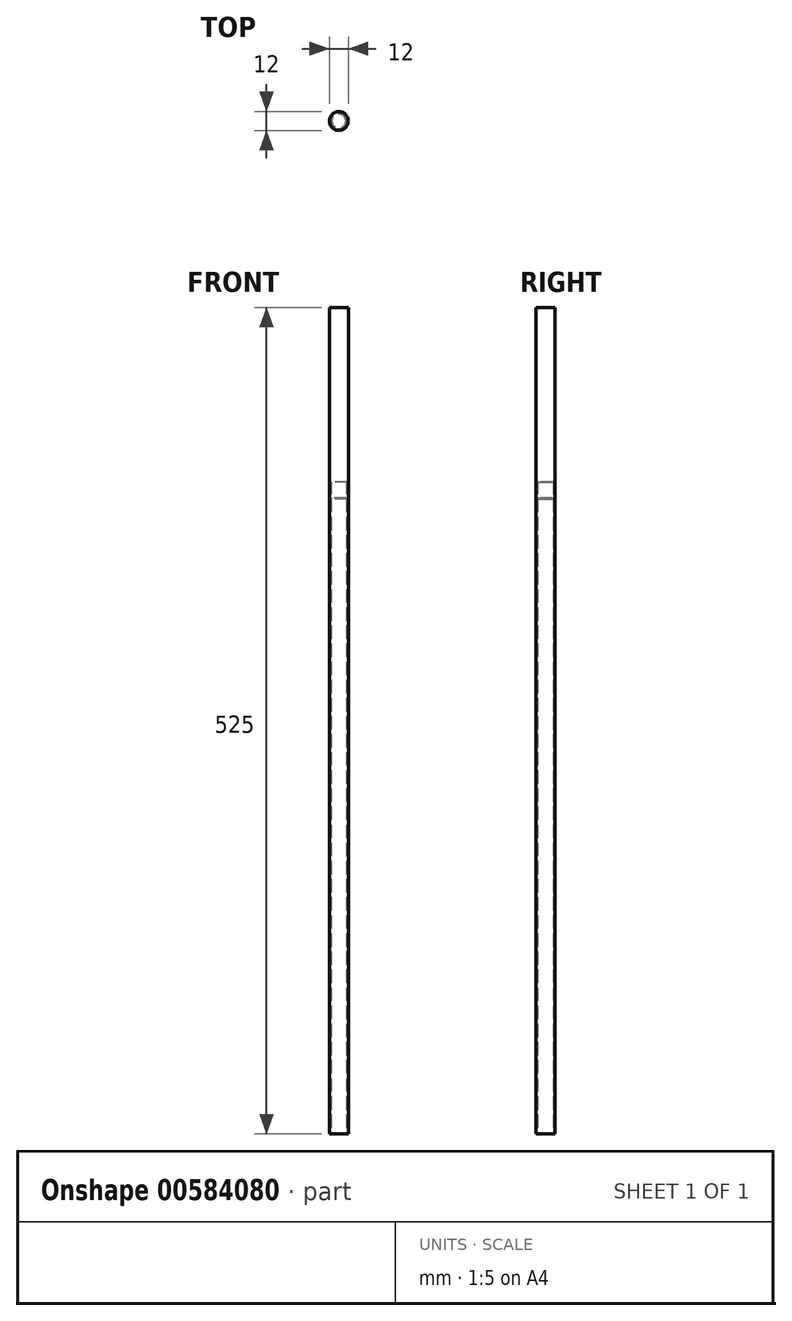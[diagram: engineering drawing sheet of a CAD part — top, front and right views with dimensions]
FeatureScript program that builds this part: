
annotation { "Feature Type Name" : "Feature", "Feature Type Description" : "" }
export const myFeature = defineFeature(function(context is Context, id is Id, definition is map)
    precondition{}
    {
        {
            var Q0;
            Q0=qCreatedBy(makeId("Top.planeOp"),FACE);
            var sketch = newSketch(context, id + "F0", { "sketchPlane" : qUnion([Q0])});
            skCircle(sketch, "E0", {"center": v(0, 0) * mm, "radius": 5 * mm});
            skCircle(sketch, "E1", {"center": v(0, 0) * mm, "radius": 6 * mm});
            skSolve(sketch);
        }
        {
            var Q0;
            Q0=makeQuery(id+"F0.imprint","IMPRINT",FACE,{"disambiguationData":[TD([[makeQuery(id+"F0.imprint","IMPRINT",EDGE,{"derivedFrom":sQuery(id+"F0.wireOp",EDGE,"E0")}),1.0]])]});
            var Q1;
            Q1=makeQuery(id+"F0.imprint","IMPRINT",FACE,{"disambiguationData":[TD([[makeQuery(id+"F0.imprint","IMPRINT",EDGE,{"derivedFrom":sQuery(id+"F0.wireOp",EDGE,"E0")}),-1.0]])]});
            extrude(context, id + "F1", {"entities" : qUnion([Q0, Q1]), "depth" : 525 * mm, "offsetDistance" : 25 * mm});
        }
        {
            var Q0;
            Q0=makeQuery(id+"F0.imprint","IMPRINT",FACE,{"disambiguationData":[TD([[makeQuery(id+"F0.imprint","IMPRINT",EDGE,{"derivedFrom":sQuery(id+"F0.wireOp",EDGE,"E0")}),1.0]])]});
            extrude(context, id + "F2", {"entities" : qUnion([Q0]), "depth" : 404 * mm, "offsetDistance" : 25 * mm});
        }
        {
            var Q0;
            Q0=makeQuery(id+"F1.opExtrude","CAP_EDGE",EDGE,{"disambiguationData":[OSD([sQuery(id+"F0.wireOp",EDGE,"E0")])],"isStart":false});
            var Q1;
            Q1=makeQuery(id+"F1.opExtrude","CAP_EDGE",EDGE,{"disambiguationData":[OSD([sQuery(id+"F0.wireOp",EDGE,"E0")])],"isStart":true});
            var Q2;
            Q2=makeQuery(id+"F2.opExtrude","CAP_EDGE",EDGE,{"disambiguationData":[OSD([sQuery(id+"F0.wireOp",EDGE,"E0")])],"isStart":true});
            var Q3;
            Q3=makeQuery(id+"F2.opExtrude","CAP_EDGE",EDGE,{"disambiguationData":[OSD([sQuery(id+"F0.wireOp",EDGE,"E0")])],"isStart":false});
            chamfer(context, id + "F3", {"entities" : qUnion([Q0, Q1, Q2, Q3]), "width" : 0.5 * mm, "tangentPropagation" : true});
        }
        {
            var Q0;
            Q0=makeQuery(id+"F0.imprint","IMPRINT",FACE,{"disambiguationData":[TD([[makeQuery(id+"F0.imprint","IMPRINT",EDGE,{"derivedFrom":sQuery(id+"F0.wireOp",EDGE,"E0")}),1.0]])]});
            extrude(context, id + "F4", {"entities" : qUnion([Q0]), "depth" : 414 * mm, "offsetDistance" : 25 * mm});
        }
    });
